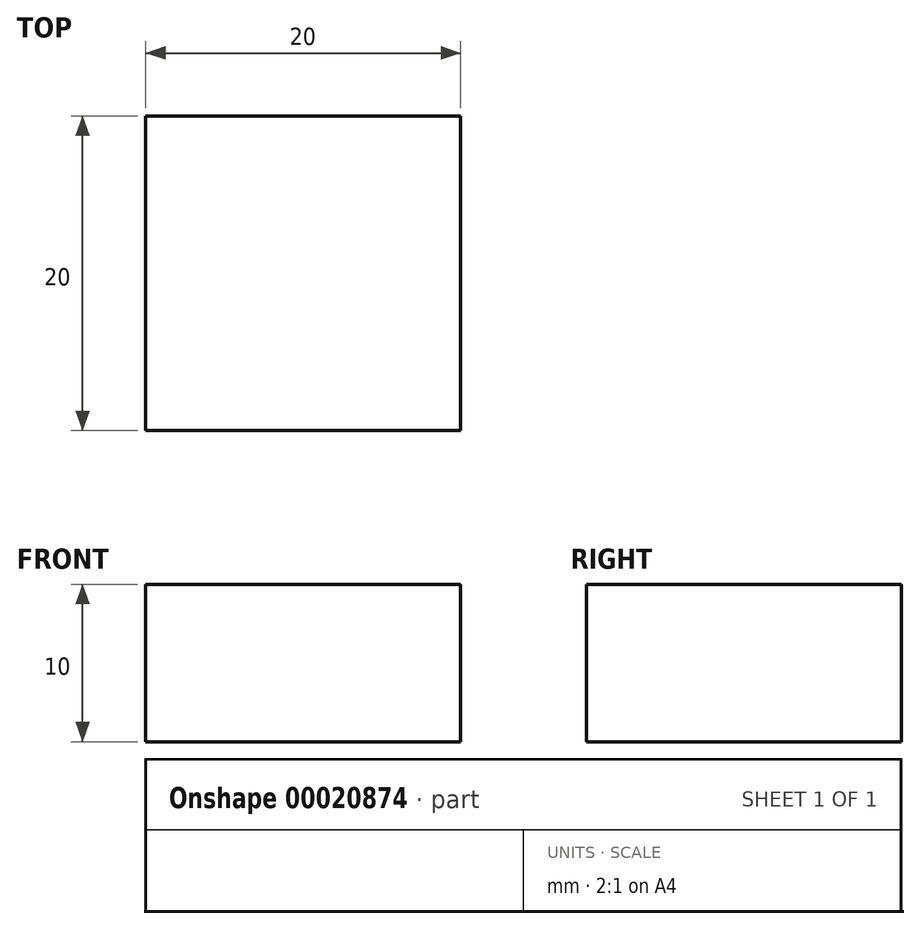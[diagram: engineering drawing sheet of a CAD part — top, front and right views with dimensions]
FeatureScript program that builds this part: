
annotation { "Feature Type Name" : "Feature", "Feature Type Description" : "" }
export const myFeature = defineFeature(function(context is Context, id is Id, definition is map)
    precondition{}
    {
        {
            var Q0;
            Q0=qCreatedBy(makeId("Top.planeOp"),FACE);
            var sketch = newSketch(context, id + "F0", { "sketchPlane" : qUnion([Q0])});
            skLineSegment(sketch, "E0.rect.bottom", {"start": v(-10, -10) * mm, "end": v(10, -10) * mm});
            skLineSegment(sketch, "E0.rect.top", {"start": v(-10, 10) * mm, "end": v(10, 10) * mm});
            skLineSegment(sketch, "E0.rect.left", {"start": v(-10, -10) * mm, "end": v(-10, 10) * mm});
            skLineSegment(sketch, "E0.rect.right", {"start": v(10, -10) * mm, "end": v(10, 10) * mm});
            skPoint(sketch, "E0.rect.middle", {"position": v(0, 0) * mm});
            skSolve(sketch);
        }
        {
            var Q0;
            Q0 = qSketchRegion(id + "F0", true);
            extrude(context, id + "F1", {"entities" : qUnion([Q0]), "depth" : 10 * mm});
        }
    });
